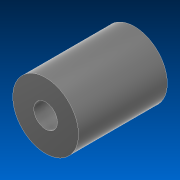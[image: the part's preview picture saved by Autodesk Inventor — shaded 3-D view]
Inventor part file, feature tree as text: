
AUTODESK INVENTOR PART (.ipt)
format: ipt  version: 2022.2 (Build 262287000, 287)  size: 91,648 bytes
history: native  units: in
note: dims shown in document units (in); Inventor stores cm internally (conversion verified against a paired STEP export)
features: extrude x1, sketch x1
ambient origin geometry x8: Origin, YZ Plane, XZ Plane, XY Plane, X Axis, Y Axis, Z Axis, Center Point
bodies: Solid1 (feature_tree)
feature tree (2):
  extrude  "Extrusion1"  Depth=0.675in
  sketch  "Sketch1"  dims[d0=0.18in d1=0.5in d2=0.675in d3=0.0in]
